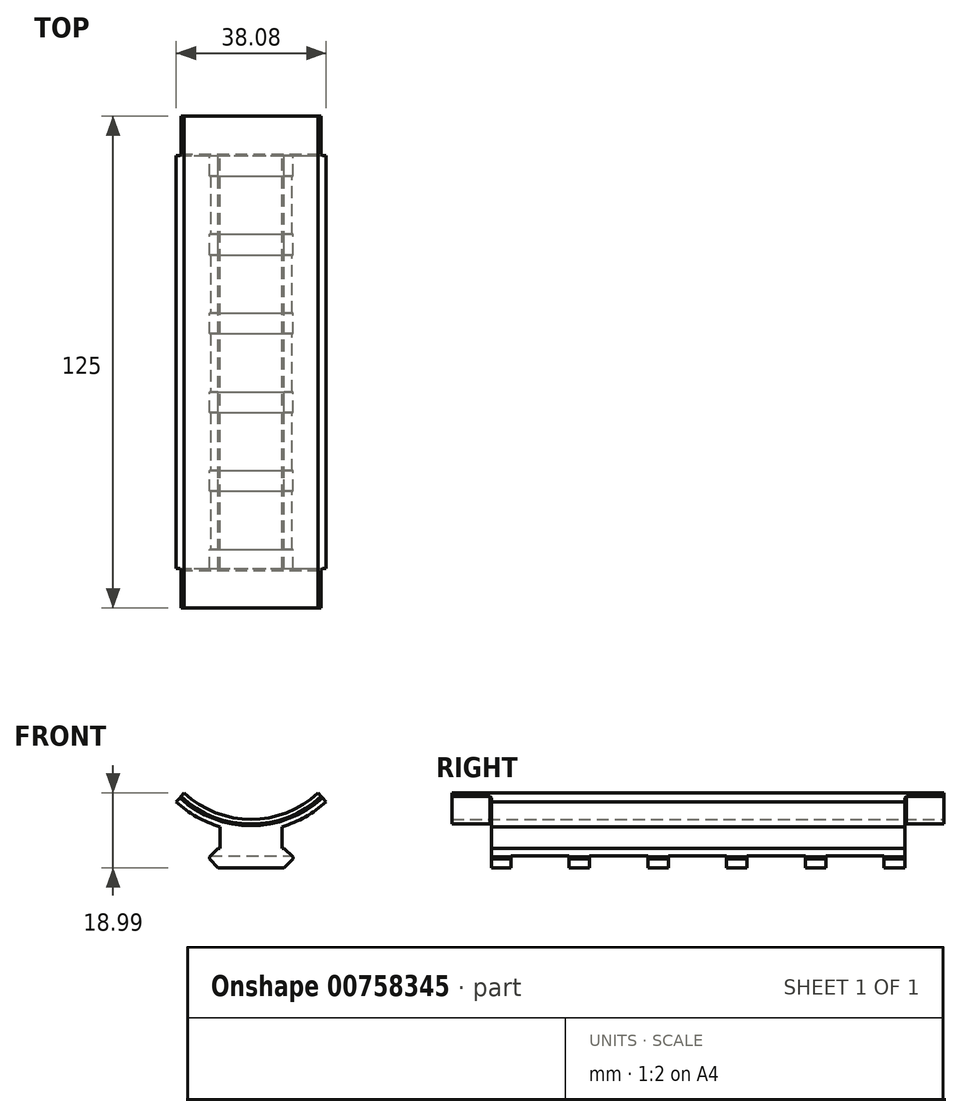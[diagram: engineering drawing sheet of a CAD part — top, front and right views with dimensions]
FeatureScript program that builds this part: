
annotation { "Feature Type Name" : "Feature", "Feature Type Description" : "" }
export const myFeature = defineFeature(function(context is Context, id is Id, definition is map)
    precondition{}
    {
        {
            var Q0;
            Q0=qCreatedBy(makeId("Front.planeOp"),FACE);
            var sketch = newSketch(context, id + "F0", { "sketchPlane" : qUnion([Q0])});
            skArc(sketch, "E0", {"start": v(-17, 0) * mm, "mid": v(0, -6.67) * mm, "end": v(17, 0) * mm});
            skArc(sketch, "E1.0", {"start": v(-19.04, -2.2) * mm, "mid": v(0, -9.67) * mm, "end": v(19.04, -2.2) * mm});
            skLineSegment(sketch, "E2", {"start": v(-19.04, -2.2) * mm, "end": v(-17, 0) * mm});
            skLineSegment(sketch, "E3", {"start": v(17, 0) * mm, "end": v(19.04, -2.2) * mm});
            skLineSegment(sketch, "E4", {"start": v(0, 24.22) * mm, "end": v(0, -34.17) * mm, "construction": true});
            skLineSegment(sketch, "E5.bottom", {"start": v(-7.84, -14.04) * mm, "end": v(7.84, -14.04) * mm});
            skLineSegment(sketch, "E5.left", {"start": v(-7.84, -14.04) * mm, "end": v(-7.84, -8.55) * mm});
            skLineSegment(sketch, "E5.right", {"start": v(7.84, -14.04) * mm, "end": v(7.84, -8.55) * mm});
            skPoint(sketch, "E6", {"position": v(0, -14.04) * mm});
            skLineSegment(sketch, "E7", {"start": v(-10.6, -16.78) * mm, "end": v(-8.4, -19) * mm});
            skLineSegment(sketch, "E8", {"start": v(-8.4, -19) * mm, "end": v(8.4, -19) * mm});
            skLineSegment(sketch, "E9", {"start": v(8.4, -19) * mm, "end": v(10.6, -16.78) * mm});
            skLineSegment(sketch, "E10", {"start": v(10.6, -16.25) * mm, "end": v(8.4, -14.04) * mm});
            skLineSegment(sketch, "E11", {"start": v(8.4, -14.04) * mm, "end": v(-8.4, -14.04) * mm});
            skLineSegment(sketch, "E12", {"start": v(-8.4, -14.04) * mm, "end": v(-10.6, -16.25) * mm});
            skLineSegment(sketch, "E13", {"start": v(-10.6, -16.25) * mm, "end": v(-10.6, -16.78) * mm});
            skLineSegment(sketch, "E14", {"start": v(10.6, -16.25) * mm, "end": v(10.6, -16.78) * mm});
            skPoint(sketch, "E15", {"position": v(0, -19) * mm});
            skLineSegment(sketch, "E16.bottom", {"start": v(-9.5, -15.14) * mm, "end": v(9.5, -15.14) * mm, "construction": true});
            skLineSegment(sketch, "E16.top", {"start": v(-9.5, -17.89) * mm, "end": v(9.5, -17.89) * mm, "construction": true});
            skLineSegment(sketch, "E16.left", {"start": v(-9.5, -15.14) * mm, "end": v(-9.5, -17.89) * mm, "construction": true});
            skLineSegment(sketch, "E16.right", {"start": v(9.5, -15.14) * mm, "end": v(9.5, -17.89) * mm, "construction": true});
            skPoint(sketch, "E17", {"position": v(0, -9.67) * mm});
            skCircle(sketch, "E18", {"center": v(3.92, -11.3) * mm, "radius": 1.5 * mm, "construction": true});
            skLineSegment(sketch, "E19", {"start": v(7.84, -11.3) * mm, "end": v(0, -11.3) * mm, "construction": true});
            skCircle(sketch, "E20.MirrorC", {"center": v(-3.92, -11.3) * mm, "radius": 1.5 * mm, "construction": true});
            skSolve(sketch);
        }
        {
            var Q0;
            Q0=makeQuery(id+"F0.imprint","IMPRINT",FACE,{"disambiguationData":[TD([[makeQuery(id+"F0.imprint","IMPRINT",EDGE,{"derivedFrom":sQuery(id+"F0.wireOp",EDGE,"E0")}),-1.0]])]});
            var Q1;
            {var subQ0=sQuery(id+"F0.wireOp",EDGE,"E5.left");Q1=makeQuery(id+"F0.imprint","IMPRINT",FACE,{"disambiguationData":[TD([[makeQuery(id+"F0.imprint","IMPRINT",EDGE,{"derivedFrom":subQ0}),-1.0]])]});}
            var Q2;
            Q2=makeQuery(id+"F0.imprint","IMPRINT",FACE,{"disambiguationData":[TD([[makeQuery(id+"F0.imprint","IMPRINT",EDGE,{"derivedFrom":sQuery(id+"F0.wireOp",EDGE,"E7")}),1.0]])]});
            extrude(context, id + "F1", {"entities" : qUnion([Q0, Q1, Q2]), "depth" : 105 * mm, "offsetDistance" : 25 * mm});
        }
        {
            var Q0;
            Q0=makeQuery(id+"F1.opExtrude","CAP_FACE",FACE,{"disambiguationData":[OSD([sQuery(id+"F0.wireOp",EDGE,"E0"),sQuery(id+"F0.wireOp",EDGE,"E1.0"),sQuery(id+"F0.wireOp",EDGE,"E2"),sQuery(id+"F0.wireOp",EDGE,"E3"),sQuery(id+"F0.wireOp",EDGE,"E5.left"),sQuery(id+"F0.wireOp",EDGE,"E5.right"),sQuery(id+"F0.wireOp",EDGE,"E7"),sQuery(id+"F0.wireOp",EDGE,"E8"),sQuery(id+"F0.wireOp",EDGE,"E9"),sQuery(id+"F0.wireOp",EDGE,"E10"),sQuery(id+"F0.wireOp",EDGE,"E11"),sQuery(id+"F0.wireOp",EDGE,"E12"),sQuery(id+"F0.wireOp",EDGE,"E13"),sQuery(id+"F0.wireOp",EDGE,"E14")])],"isStart":true});
            var sketch = newSketch(context, id + "F2", { "sketchPlane" : qUnion([Q0])});
            skArc(sketch, "E21.0", {"start": v(17, 0) * mm, "mid": v(0, -6.67) * mm, "end": v(-17, 0) * mm});
            skArc(sketch, "E22.0", {"start": v(17.82, -0.88) * mm, "mid": v(0, -7.87) * mm, "end": v(-17.82, -0.88) * mm});
            skLineSegment(sketch, "E23", {"start": v(-17.82, -0.88) * mm, "end": v(-17, 0) * mm});
            skLineSegment(sketch, "E24", {"start": v(17.82, -0.88) * mm, "end": v(17, 0) * mm});
            skSolve(sketch);
        }
        {
            var Q0;
            Q0 = qSketchRegion(id + "F2", true);
            extrude(context, id + "F3", {"entities" : qUnion([Q0]), "operationType" : NewBodyOperationType.ADD, "depth" : 10 * mm, "offsetDistance" : 25 * mm, "hasSecondDirection" : true, "secondDirectionOppositeDirection" : true, "secondDirectionDepth" : 115 * mm});
        }
        {
            var Q0;
            Q0=qCreatedBy(makeId("Right.planeOp"),FACE);
            var sketch = newSketch(context, id + "F4", { "sketchPlane" : qUnion([Q0])});
            skLineSegment(sketch, "E25.0.6", {"start": v(0, -14.04) * mm, "end": v(0, -16.25) * mm, "construction": true});
            skLineSegment(sketch, "E25.0.7", {"start": v(0, -16.25) * mm, "end": v(0, -16.78) * mm, "construction": true});
            skLineSegment(sketch, "E25.0.8", {"start": v(0, -16.78) * mm, "end": v(0, -19) * mm, "construction": true});
            skLineSegment(sketch, "E25.0.10", {"start": v(0, -19) * mm, "end": v(0, -16.78) * mm, "construction": true});
            skLineSegment(sketch, "E25.0.11", {"start": v(0, -16.78) * mm, "end": v(0, -16.25) * mm, "construction": true});
            skLineSegment(sketch, "E25.0.12", {"start": v(0, -16.25) * mm, "end": v(0, -14.04) * mm, "construction": true});
            skLineSegment(sketch, "E26.0", {"start": v(-105, -19) * mm, "end": v(0, -19) * mm, "construction": true});
            skLineSegment(sketch, "E27.bottom", {"start": v(-5.23, -19) * mm, "end": v(-20.02, -19) * mm});
            skLineSegment(sketch, "E27.top", {"start": v(-5.23, -16) * mm, "end": v(-20.02, -16) * mm});
            skLineSegment(sketch, "E27.left", {"start": v(-5.23, -19) * mm, "end": v(-5.23, -16) * mm});
            skLineSegment(sketch, "E27.right", {"start": v(-20.02, -19) * mm, "end": v(-20.02, -16) * mm});
            skPoint(sketch, "E28", {"position": v(-12.62, -16) * mm});
            skLineSegment(sketch, "E29", {"start": v(-5.23, -16) * mm, "end": v(0, -16) * mm, "construction": true});
            skPoint(sketch, "E30", {"position": v(-2.62, -16) * mm});
            skLineSegment(sketch, "E31.1.0.0", {"start": v(-25.25, -16) * mm, "end": v(-20.02, -16) * mm, "construction": true});
            skLineSegment(sketch, "E31.1.0.1", {"start": v(-25.25, -19) * mm, "end": v(-25.25, -16) * mm});
            skLineSegment(sketch, "E31.1.0.2", {"start": v(-25.25, -16) * mm, "end": v(-40.03, -16) * mm});
            skLineSegment(sketch, "E31.1.0.3", {"start": v(-40.03, -19) * mm, "end": v(-40.03, -16) * mm});
            skLineSegment(sketch, "E31.1.0.4", {"start": v(-25.25, -19) * mm, "end": v(-40.03, -19) * mm});
            skLineSegment(sketch, "E31.2.0.0", {"start": v(-45.26, -16) * mm, "end": v(-40.03, -16) * mm, "construction": true});
            skLineSegment(sketch, "E31.2.0.1", {"start": v(-45.26, -19) * mm, "end": v(-45.26, -16) * mm});
            skLineSegment(sketch, "E31.2.0.2", {"start": v(-45.26, -16) * mm, "end": v(-60.05, -16) * mm});
            skLineSegment(sketch, "E31.2.0.3", {"start": v(-60.05, -19) * mm, "end": v(-60.05, -16) * mm});
            skLineSegment(sketch, "E31.2.0.4", {"start": v(-45.26, -19) * mm, "end": v(-60.05, -19) * mm});
            skLineSegment(sketch, "E31.direction1", {"start": v(-25.25, -16) * mm, "end": v(-5.23, -16) * mm, "construction": true});
            skLineSegment(sketch, "E32.0.3.0", {"start": v(-65.28, -16) * mm, "end": v(-60.05, -16) * mm, "construction": true});
            skLineSegment(sketch, "E32.3.3.0", {"start": v(-65.28, -19) * mm, "end": v(-65.28, -16) * mm});
            skLineSegment(sketch, "E32.6.3.0", {"start": v(-65.28, -16) * mm, "end": v(-80.06, -16) * mm});
            skLineSegment(sketch, "E32.9.3.0", {"start": v(-80.06, -19) * mm, "end": v(-80.06, -16) * mm});
            skLineSegment(sketch, "E32.12.3.0", {"start": v(-65.28, -19) * mm, "end": v(-80.06, -19) * mm});
            skLineSegment(sketch, "E32.0.4.0", {"start": v(-85.3, -16) * mm, "end": v(-80.06, -16) * mm, "construction": true});
            skLineSegment(sketch, "E32.3.4.0", {"start": v(-85.3, -19) * mm, "end": v(-85.3, -16) * mm});
            skLineSegment(sketch, "E32.6.4.0", {"start": v(-85.3, -16) * mm, "end": v(-100.08, -16) * mm});
            skLineSegment(sketch, "E32.9.4.0", {"start": v(-100.08, -19) * mm, "end": v(-100.08, -16) * mm});
            skLineSegment(sketch, "E32.12.4.0", {"start": v(-85.3, -19) * mm, "end": v(-100.08, -19) * mm});
            skLineSegment(sketch, "E32.0.5.0", {"start": v(-105.3, -16) * mm, "end": v(-100.08, -16) * mm, "construction": true});
            skLineSegment(sketch, "E32.3.5.0", {"start": v(-105.3, -19) * mm, "end": v(-105.3, -16) * mm});
            skLineSegment(sketch, "E32.6.5.0", {"start": v(-105.3, -16) * mm, "end": v(-120.1, -16) * mm});
            skLineSegment(sketch, "E32.9.5.0", {"start": v(-120.1, -19) * mm, "end": v(-120.1, -16) * mm});
            skLineSegment(sketch, "E32.12.5.0", {"start": v(-105.3, -19) * mm, "end": v(-120.1, -19) * mm});
            skSolve(sketch);
        }
        {
            var Q0;
            Q0 = qSketchRegion(id + "F4", true);
            extrude(context, id + "F5", {"entities" : qUnion([Q0]), "operationType" : NewBodyOperationType.REMOVE, "endBound" : BoundingType.SYMMETRIC, "oppositeDirection" : true, "depth" : 25 * mm, "offsetDistance" : 25 * mm});
        }
        {
            var Q0;
            Q0=makeQuery(id+"F3.boolean.opBoolean","INTERSECT",EDGE,{"derivedFrom":[makeQuery(id+"F1.opExtrude","CAP_FACE",FACE,{"disambiguationData":[OSD([sQuery(id+"F0.wireOp",EDGE,"E0"),sQuery(id+"F0.wireOp",EDGE,"E1.0"),sQuery(id+"F0.wireOp",EDGE,"E2"),sQuery(id+"F0.wireOp",EDGE,"E3"),sQuery(id+"F0.wireOp",EDGE,"E5.left"),sQuery(id+"F0.wireOp",EDGE,"E5.right"),sQuery(id+"F0.wireOp",EDGE,"E7"),sQuery(id+"F0.wireOp",EDGE,"E8"),sQuery(id+"F0.wireOp",EDGE,"E9"),sQuery(id+"F0.wireOp",EDGE,"E10"),sQuery(id+"F0.wireOp",EDGE,"E11"),sQuery(id+"F0.wireOp",EDGE,"E12"),sQuery(id+"F0.wireOp",EDGE,"E13"),sQuery(id+"F0.wireOp",EDGE,"E14")])],"isStart":true}),makeQuery(id+"F3.opExtrude","SWEPT_FACE",FACE,{"disambiguationData":[OSD([sQuery(id+"F2.wireOp",EDGE,"E22.0")])]})]});
            var Q1;
            Q1=makeQuery(id+"F3.boolean.opBoolean","INTERSECT",EDGE,{"derivedFrom":[makeQuery(id+"F1.opExtrude","CAP_FACE",FACE,{"disambiguationData":[OSD([sQuery(id+"F0.wireOp",EDGE,"E0"),sQuery(id+"F0.wireOp",EDGE,"E1.0"),sQuery(id+"F0.wireOp",EDGE,"E2"),sQuery(id+"F0.wireOp",EDGE,"E3"),sQuery(id+"F0.wireOp",EDGE,"E5.left"),sQuery(id+"F0.wireOp",EDGE,"E5.right"),sQuery(id+"F0.wireOp",EDGE,"E7"),sQuery(id+"F0.wireOp",EDGE,"E8"),sQuery(id+"F0.wireOp",EDGE,"E9"),sQuery(id+"F0.wireOp",EDGE,"E10"),sQuery(id+"F0.wireOp",EDGE,"E11"),sQuery(id+"F0.wireOp",EDGE,"E12"),sQuery(id+"F0.wireOp",EDGE,"E13"),sQuery(id+"F0.wireOp",EDGE,"E14")])],"isStart":false}),makeQuery(id+"F3.opExtrude","SWEPT_FACE",FACE,{"disambiguationData":[OSD([sQuery(id+"F2.wireOp",EDGE,"E22.0")])]})]});
            chamfer(context, id + "F6", {"entities" : qUnion([Q0, Q1]), "width" : 0.4 * mm, "tangentPropagation" : true});
        }
    });
